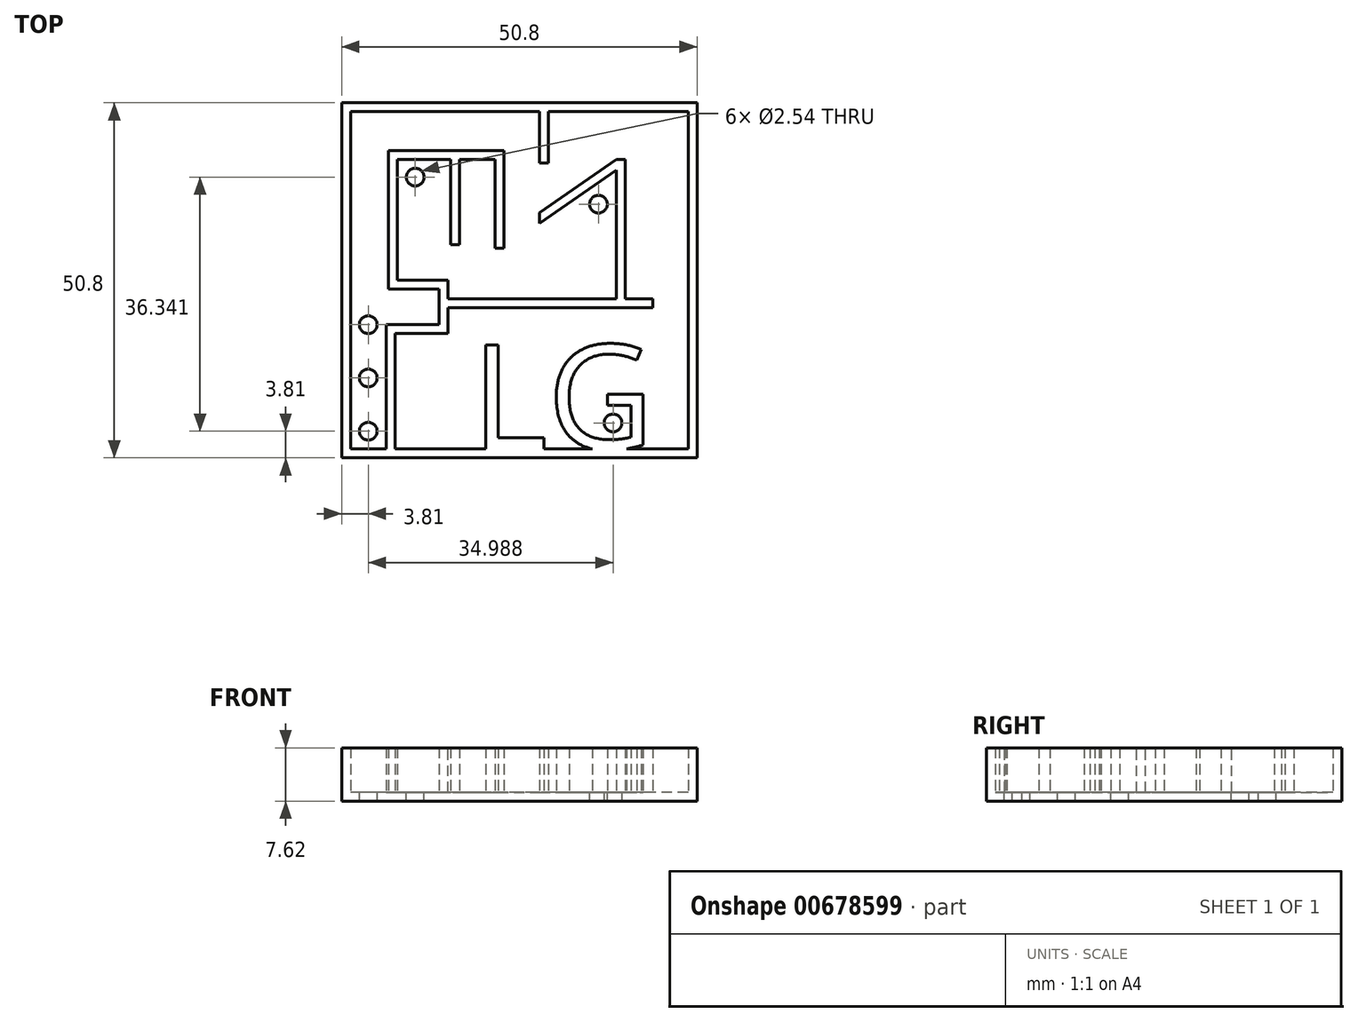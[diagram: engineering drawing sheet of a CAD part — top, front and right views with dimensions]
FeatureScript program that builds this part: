
annotation { "Feature Type Name" : "Feature", "Feature Type Description" : "" }
export const myFeature = defineFeature(function(context is Context, id is Id, definition is map)
    precondition{}
    {
        {
            var Q0;
            Q0=qCreatedBy(makeId("Top.planeOp"),FACE);
            var sketch = newSketch(context, id + "F0", { "sketchPlane" : qUnion([Q0])});
            skLineSegment(sketch, "E0.bottom", {"start": v(0, 0) * mm, "end": v(-50.8, 0) * mm});
            skLineSegment(sketch, "E0.top", {"start": v(0, 50.8) * mm, "end": v(-50.8, 50.8) * mm});
            skLineSegment(sketch, "E0.left", {"start": v(0, 0) * mm, "end": v(0, 50.8) * mm});
            skLineSegment(sketch, "E0.right", {"start": v(-50.8, 0) * mm, "end": v(-50.8, 50.8) * mm});
            skSolve(sketch);
        }
        {
            var Q0;
            Q0=makeQuery(id+"F0.imprint","IMPRINT",FACE,{"disambiguationData":[TD([[makeQuery(id+"F0.imprint","IMPRINT",EDGE,{"derivedFrom":sQuery(id+"F0.wireOp",EDGE,"E0.bottom")}),-1.0]])]});
            extrude(context, id + "F1", {"entities" : qUnion([Q0]), "depth" : 7.62 * mm, "offsetDistance" : 25.4 * mm});
        }
        {
            var Q0;
            Q0=makeQuery(id+"F1.opExtrude","CAP_FACE",FACE,{"disambiguationData":[OSD([sQuery(id+"F0.wireOp",EDGE,"E0.bottom"),sQuery(id+"F0.wireOp",EDGE,"E0.top"),sQuery(id+"F0.wireOp",EDGE,"E0.left"),sQuery(id+"F0.wireOp",EDGE,"E0.right")])],"isStart":false});
            shell(context, id + "F2", {"entities" : qUnion([Q0]), "thickness" : 1.27 * mm});
        }
        {
            var Q0;
            Q0=makeQuery(id+"F2.opShell","OFFSET_FACE",FACE,{"disambiguationData":[OSD([sQuery(id+"F0.wireOp",EDGE,"E0.bottom"),sQuery(id+"F0.wireOp",EDGE,"E0.top"),sQuery(id+"F0.wireOp",EDGE,"E0.left"),sQuery(id+"F0.wireOp",EDGE,"E0.right")])]});
            var sketch = newSketch(context, id + "F3", { "sketchPlane" : qUnion([Q0])});
            skLineSegment(sketch, "E1", {"start": v(-49.53, 1.27) * mm, "end": v(-44.45, 1.27) * mm});
            skLineSegment(sketch, "E2", {"start": v(-44.45, 1.27) * mm, "end": v(-44.45, 19.05) * mm});
            skLineSegment(sketch, "E3", {"start": v(-44.45, 19.05) * mm, "end": v(-43.18, 19.05) * mm});
            skLineSegment(sketch, "E4", {"start": v(-43.18, 19.05) * mm, "end": v(-43.18, 1.27) * mm});
            skSolve(sketch);
        }
        {
            var Q0;
            {var subQ0=sQuery(id+"F3.wireOp",EDGE,"E2");Q0=makeQuery(id+"F3.imprint","IMPRINT",FACE,{"disambiguationData":[TD([[makeQuery(id+"F3.imprint","IMPRINT",EDGE,{"derivedFrom":subQ0}),-1.0]])]});}
            extrude(context, id + "F4", {"entities" : qUnion([Q0]), "operationType" : NewBodyOperationType.ADD, "depth" : 6.35 * mm, "offsetDistance" : 25.4 * mm});
        }
        {
            var Q0;
            Q0=makeQuery(id+"F2.opShell","OFFSET_FACE",FACE,{"disambiguationData":[OSD([sQuery(id+"F0.wireOp",EDGE,"E0.bottom"),sQuery(id+"F0.wireOp",EDGE,"E0.top"),sQuery(id+"F0.wireOp",EDGE,"E0.left"),sQuery(id+"F0.wireOp",EDGE,"E0.right")])]});
            var sketch = newSketch(context, id + "F5", { "sketchPlane" : qUnion([Q0])});
            skLineSegment(sketch, "E5.bottom", {"start": v(-43.18, 19.05) * mm, "end": v(-35.6, 19.05) * mm});
            skLineSegment(sketch, "E5.top", {"start": v(-43.18, 17.78) * mm, "end": v(-35.6, 17.78) * mm});
            skLineSegment(sketch, "E5.left", {"start": v(-43.18, 19.05) * mm, "end": v(-43.18, 17.78) * mm});
            skLineSegment(sketch, "E5.right", {"start": v(-35.6, 19.05) * mm, "end": v(-35.6, 17.78) * mm});
            skSolve(sketch);
        }
        {
            var Q0;
            Q0 = qSketchRegion(id + "F5", true);
            extrude(context, id + "F6", {"entities" : qUnion([Q0]), "operationType" : NewBodyOperationType.ADD, "depth" : 6.35 * mm, "offsetDistance" : 25.4 * mm});
        }
        {
            var Q0;
            Q0=makeQuery(id+"F2.opShell","OFFSET_FACE",FACE,{"disambiguationData":[OSD([sQuery(id+"F0.wireOp",EDGE,"E0.bottom"),sQuery(id+"F0.wireOp",EDGE,"E0.top"),sQuery(id+"F0.wireOp",EDGE,"E0.left"),sQuery(id+"F0.wireOp",EDGE,"E0.right")])]});
            var sketch = newSketch(context, id + "F7", { "sketchPlane" : qUnion([Q0])});
            skLineSegment(sketch, "E6.bottom", {"start": v(-35.6, 19.05) * mm, "end": v(-36.86, 19.05) * mm});
            skLineSegment(sketch, "E6.top", {"start": v(-35.6, 24.13) * mm, "end": v(-36.86, 24.13) * mm});
            skLineSegment(sketch, "E6.left", {"start": v(-35.6, 19.05) * mm, "end": v(-35.6, 24.13) * mm});
            skLineSegment(sketch, "E6.right", {"start": v(-36.86, 19.05) * mm, "end": v(-36.86, 24.13) * mm});
            skSolve(sketch);
        }
        {
            var Q0;
            Q0=makeQuery(id+"F7.imprint","IMPRINT",FACE,{"disambiguationData":[TD([[makeQuery(id+"F7.imprint","IMPRINT",EDGE,{"derivedFrom":sQuery(id+"F7.wireOp",EDGE,"E6.bottom")}),1.0]])]});
            extrude(context, id + "F8", {"entities" : qUnion([Q0]), "operationType" : NewBodyOperationType.ADD, "depth" : 6.35 * mm, "offsetDistance" : 25.4 * mm});
        }
        {
            var Q0;
            Q0=makeQuery(id+"F2.opShell","OFFSET_FACE",FACE,{"disambiguationData":[OSD([sQuery(id+"F0.wireOp",EDGE,"E0.bottom"),sQuery(id+"F0.wireOp",EDGE,"E0.top"),sQuery(id+"F0.wireOp",EDGE,"E0.left"),sQuery(id+"F0.wireOp",EDGE,"E0.right")])]});
            var sketch = newSketch(context, id + "F9", { "sketchPlane" : qUnion([Q0])});
            skLineSegment(sketch, "E7.bottom", {"start": v(-35.6, 24.13) * mm, "end": v(-44.09, 24.13) * mm});
            skLineSegment(sketch, "E7.top", {"start": v(-35.6, 25.4) * mm, "end": v(-44.09, 25.4) * mm});
            skLineSegment(sketch, "E7.left", {"start": v(-35.6, 24.13) * mm, "end": v(-35.6, 25.4) * mm});
            skLineSegment(sketch, "E7.right", {"start": v(-44.09, 24.13) * mm, "end": v(-44.09, 25.4) * mm});
            skSolve(sketch);
        }
        {
            var Q0;
            Q0=makeQuery(id+"F9.imprint","IMPRINT",FACE,{"disambiguationData":[TD([[makeQuery(id+"F9.imprint","IMPRINT",EDGE,{"derivedFrom":sQuery(id+"F9.wireOp",EDGE,"E7.top")}),1.0]])]});
            extrude(context, id + "F10", {"entities" : qUnion([Q0]), "operationType" : NewBodyOperationType.ADD, "depth" : 6.35 * mm, "offsetDistance" : 25.4 * mm});
        }
        {
            var Q0;
            Q0=makeQuery(id+"F2.opShell","OFFSET_FACE",FACE,{"disambiguationData":[OSD([sQuery(id+"F0.wireOp",EDGE,"E0.bottom"),sQuery(id+"F0.wireOp",EDGE,"E0.top"),sQuery(id+"F0.wireOp",EDGE,"E0.left"),sQuery(id+"F0.wireOp",EDGE,"E0.right")])]});
            var sketch = newSketch(context, id + "F11", { "sketchPlane" : qUnion([Q0])});
            skCircle(sketch, "E8", {"center": v(-47, 3.81) * mm, "radius": 1.27 * mm});
            skSolve(sketch);
        }
        {
            var Q0;
            Q0=makeQuery(id+"F11.imprint","IMPRINT",FACE,{"disambiguationData":[TD([[makeQuery(id+"F11.imprint","IMPRINT",EDGE,{"derivedFrom":sQuery(id+"F11.wireOp",EDGE,"E8")}),-1.0]])]});
            var sketch = newSketch(context, id + "F12", { "sketchPlane" : qUnion([Q0])});
            skCircle(sketch, "E9", {"center": v(-47, 11.43) * mm, "radius": 1.27 * mm});
            skSolve(sketch);
        }
        {
            var Q0;
            Q0 = qSketchRegion(id + "F12", true);
            var Q1;
            Q1=makeQuery(id+"F11.imprint","IMPRINT",FACE,{"disambiguationData":[TD([[makeQuery(id+"F11.imprint","IMPRINT",EDGE,{"derivedFrom":sQuery(id+"F11.wireOp",EDGE,"E8")}),1.0]])]});
            extrude(context, id + "F13", {"entities" : qUnion([Q0, Q1]), "operationType" : NewBodyOperationType.REMOVE, "oppositeDirection" : true, "depth" : 25.4 * mm, "offsetDistance" : 25.4 * mm});
        }
        {
            var Q0;
            Q0=makeQuery(id+"F2.opShell","OFFSET_FACE",FACE,{"disambiguationData":[OSD([sQuery(id+"F0.wireOp",EDGE,"E0.bottom"),sQuery(id+"F0.wireOp",EDGE,"E0.top"),sQuery(id+"F0.wireOp",EDGE,"E0.left"),sQuery(id+"F0.wireOp",EDGE,"E0.right")])]});
            var sketch = newSketch(context, id + "F14", { "sketchPlane" : qUnion([Q0])});
            skLineSegment(sketch, "E10.bottom", {"start": v(-44.09, 25.4) * mm, "end": v(-42.82, 25.4) * mm});
            skLineSegment(sketch, "E10.top", {"start": v(-44.09, 42.7) * mm, "end": v(-42.82, 42.7) * mm});
            skLineSegment(sketch, "E10.left", {"start": v(-44.09, 25.4) * mm, "end": v(-44.09, 42.7) * mm});
            skLineSegment(sketch, "E10.right", {"start": v(-42.82, 25.4) * mm, "end": v(-42.82, 42.7) * mm});
            skSolve(sketch);
        }
        {
            var Q0;
            Q0=makeQuery(id+"F14.imprint","IMPRINT",FACE,{"disambiguationData":[TD([[makeQuery(id+"F14.imprint","IMPRINT",EDGE,{"derivedFrom":sQuery(id+"F14.wireOp",EDGE,"E10.bottom")}),-1.0]])]});
            extrude(context, id + "F15", {"entities" : qUnion([Q0]), "operationType" : NewBodyOperationType.ADD, "depth" : 6.35 * mm, "offsetDistance" : 25.4 * mm});
        }
        {
            var Q0;
            Q0=makeQuery(id+"F2.opShell","OFFSET_FACE",FACE,{"disambiguationData":[OSD([sQuery(id+"F0.wireOp",EDGE,"E0.bottom"),sQuery(id+"F0.wireOp",EDGE,"E0.top"),sQuery(id+"F0.wireOp",EDGE,"E0.left"),sQuery(id+"F0.wireOp",EDGE,"E0.right")])]});
            var sketch = newSketch(context, id + "F16", { "sketchPlane" : qUnion([Q0])});
            skLineSegment(sketch, "E11.bottom", {"start": v(-44.09, 42.7) * mm, "end": v(-28.85, 42.7) * mm});
            skLineSegment(sketch, "E11.top", {"start": v(-44.09, 43.96) * mm, "end": v(-28.85, 43.96) * mm});
            skLineSegment(sketch, "E11.left", {"start": v(-44.09, 42.7) * mm, "end": v(-44.09, 43.96) * mm});
            skLineSegment(sketch, "E11.right", {"start": v(-28.85, 42.7) * mm, "end": v(-28.85, 43.96) * mm});
            skSolve(sketch);
        }
        {
            var Q0;
            Q0=makeQuery(id+"F16.imprint","IMPRINT",FACE,{"disambiguationData":[TD([[makeQuery(id+"F16.imprint","IMPRINT",EDGE,{"derivedFrom":sQuery(id+"F16.wireOp",EDGE,"E11.top")}),-1.0]])]});
            extrude(context, id + "F17", {"entities" : qUnion([Q0]), "operationType" : NewBodyOperationType.ADD, "depth" : 6.35 * mm, "offsetDistance" : 25.4 * mm});
        }
        {
            var Q0;
            Q0=makeQuery(id+"F2.opShell","OFFSET_FACE",FACE,{"disambiguationData":[OSD([sQuery(id+"F0.wireOp",EDGE,"E0.bottom"),sQuery(id+"F0.wireOp",EDGE,"E0.top"),sQuery(id+"F0.wireOp",EDGE,"E0.left"),sQuery(id+"F0.wireOp",EDGE,"E0.right")])]});
            var sketch = newSketch(context, id + "F18", { "sketchPlane" : qUnion([Q0])});
            skLineSegment(sketch, "E12.bottom", {"start": v(-28.85, 43.96) * mm, "end": v(-27.58, 43.96) * mm});
            skLineSegment(sketch, "E12.top", {"start": v(-28.85, 30) * mm, "end": v(-27.58, 30) * mm});
            skLineSegment(sketch, "E12.left", {"start": v(-28.85, 43.96) * mm, "end": v(-28.85, 30) * mm});
            skLineSegment(sketch, "E12.right", {"start": v(-27.58, 43.96) * mm, "end": v(-27.58, 30) * mm});
            skSolve(sketch);
        }
        {
            var Q0;
            {var subQ1=sQuery(id+"F18.wireOp",EDGE,"E12.bottom");Q0=makeQuery(id+"F18.imprint","IMPRINT",FACE,{"disambiguationData":[TD([[makeQuery(id+"F18.imprint","IMPRINT",EDGE,{"derivedFrom":subQ1}),-1.0]])]});}
            extrude(context, id + "F19", {"entities" : qUnion([Q0]), "operationType" : NewBodyOperationType.ADD, "depth" : 6.35 * mm, "offsetDistance" : 25.4 * mm});
        }
        {
            var Q0;
            Q0=makeQuery(id+"F2.opShell","OFFSET_FACE",FACE,{"disambiguationData":[OSD([sQuery(id+"F0.wireOp",EDGE,"E0.bottom"),sQuery(id+"F0.wireOp",EDGE,"E0.top"),sQuery(id+"F0.wireOp",EDGE,"E0.left"),sQuery(id+"F0.wireOp",EDGE,"E0.right")])]});
            var sketch = newSketch(context, id + "F20", { "sketchPlane" : qUnion([Q0])});
            skText(sketch, "E13", { "text": "LG", "fontName": "OpenSans-Regular.ttf"});
            const initialGuessF20  = {"E13": [-0.03222, 0.00127, 1, 0, 0.01502]};
            skSetInitialGuess(sketch, initialGuessF20);
            skSolve(sketch);
        }
        {
            var Q0;
            Q0 = qSketchRegion(id + "F20", true);
            extrude(context, id + "F21", {"entities" : qUnion([Q0]), "operationType" : NewBodyOperationType.ADD, "depth" : 6.35 * mm, "offsetDistance" : 25.4 * mm});
        }
        {
            var Q0;
            Q0=makeQuery(id+"F2.opShell","OFFSET_FACE",FACE,{"disambiguationData":[OSD([sQuery(id+"F0.wireOp",EDGE,"E0.bottom"),sQuery(id+"F0.wireOp",EDGE,"E0.top"),sQuery(id+"F0.wireOp",EDGE,"E0.left"),sQuery(id+"F0.wireOp",EDGE,"E0.right")])]});
            var sketch = newSketch(context, id + "F22", { "sketchPlane" : qUnion([Q0])});
            skCircle(sketch, "E14", {"center": v(-12, 4.98) * mm, "radius": 1.27 * mm});
            skSolve(sketch);
        }
        {
            var Q0;
            Q0 = qSketchRegion(id + "F22", true);
            extrude(context, id + "F23", {"entities" : qUnion([Q0]), "operationType" : NewBodyOperationType.REMOVE, "oppositeDirection" : true, "depth" : 25.4 * mm, "offsetDistance" : 25.4 * mm});
        }
        {
            var Q0;
            Q0=makeQuery(id+"F2.opShell","OFFSET_FACE",FACE,{"disambiguationData":[OSD([sQuery(id+"F0.wireOp",EDGE,"E0.bottom"),sQuery(id+"F0.wireOp",EDGE,"E0.top"),sQuery(id+"F0.wireOp",EDGE,"E0.left"),sQuery(id+"F0.wireOp",EDGE,"E0.right")])]});
            var sketch = newSketch(context, id + "F24", { "sketchPlane" : qUnion([Q0])});
            skCircle(sketch, "E15", {"center": v(-47, 19.05) * mm, "radius": 1.27 * mm});
            skSolve(sketch);
        }
        {
            var Q0;
            Q0 = qSketchRegion(id + "F24", true);
            extrude(context, id + "F25", {"entities" : qUnion([Q0]), "operationType" : NewBodyOperationType.REMOVE, "oppositeDirection" : true, "depth" : 25.4 * mm, "offsetDistance" : 25.4 * mm});
        }
        {
            var Q0;
            Q0=makeQuery(id+"F2.opShell","OFFSET_FACE",FACE,{"disambiguationData":[OSD([sQuery(id+"F0.wireOp",EDGE,"E0.bottom"),sQuery(id+"F0.wireOp",EDGE,"E0.top"),sQuery(id+"F0.wireOp",EDGE,"E0.left"),sQuery(id+"F0.wireOp",EDGE,"E0.right")])]});
            var sketch = newSketch(context, id + "F26", { "sketchPlane" : qUnion([Q0])});
            skLineSegment(sketch, "E16", {"start": v(-27.58, 30) * mm, "end": v(-10.82, 41.65) * mm});
            skLineSegment(sketch, "E17", {"start": v(-10.82, 41.65) * mm, "end": v(-11.55, 42.7) * mm});
            skLineSegment(sketch, "E18", {"start": v(-11.55, 42.7) * mm, "end": v(-27.58, 31.54) * mm});
            skSolve(sketch);
        }
        {
            var Q0;
            {var subQ0=sQuery(id+"F26.wireOp",EDGE,"E16");Q0=makeQuery(id+"F26.imprint","IMPRINT",FACE,{"disambiguationData":[TD([[makeQuery(id+"F26.imprint","IMPRINT",EDGE,{"derivedFrom":subQ0}),1.0]])]});}
            extrude(context, id + "F27", {"entities" : qUnion([Q0]), "operationType" : NewBodyOperationType.ADD, "depth" : 6.35 * mm, "offsetDistance" : 25.4 * mm});
        }
        {
            var Q0;
            Q0=makeQuery(id+"F2.opShell","OFFSET_FACE",FACE,{"disambiguationData":[OSD([sQuery(id+"F0.wireOp",EDGE,"E0.bottom"),sQuery(id+"F0.wireOp",EDGE,"E0.top"),sQuery(id+"F0.wireOp",EDGE,"E0.left"),sQuery(id+"F0.wireOp",EDGE,"E0.right")])]});
            var sketch = newSketch(context, id + "F28", { "sketchPlane" : qUnion([Q0])});
            skCircle(sketch, "E19", {"center": v(-40.28, 40.15) * mm, "radius": 1.27 * mm});
            skSolve(sketch);
        }
        {
            var Q0;
            Q0=makeQuery(id+"F28.imprint","IMPRINT",FACE,{"disambiguationData":[TD([[makeQuery(id+"F28.imprint","IMPRINT",EDGE,{"derivedFrom":sQuery(id+"F28.wireOp",EDGE,"E19")}),1.0]])]});
            extrude(context, id + "F29", {"entities" : qUnion([Q0]), "operationType" : NewBodyOperationType.REMOVE, "oppositeDirection" : true, "depth" : 25.4 * mm, "offsetDistance" : 25.4 * mm});
        }
        {
            var Q0;
            Q0=makeQuery(id+"F2.opShell","OFFSET_FACE",FACE,{"disambiguationData":[OSD([sQuery(id+"F0.wireOp",EDGE,"E0.bottom"),sQuery(id+"F0.wireOp",EDGE,"E0.top"),sQuery(id+"F0.wireOp",EDGE,"E0.left"),sQuery(id+"F0.wireOp",EDGE,"E0.right")])]});
            var sketch = newSketch(context, id + "F30", { "sketchPlane" : qUnion([Q0])});
            skLineSegment(sketch, "E20.bottom", {"start": v(-11.55, 42.7) * mm, "end": v(-10.28, 42.7) * mm});
            skLineSegment(sketch, "E20.top", {"start": v(-11.55, 30) * mm, "end": v(-10.28, 30) * mm});
            skLineSegment(sketch, "E20.left", {"start": v(-11.55, 42.7) * mm, "end": v(-11.55, 30) * mm});
            skLineSegment(sketch, "E20.right", {"start": v(-10.28, 42.7) * mm, "end": v(-10.28, 30) * mm});
            skSolve(sketch);
        }
        {
            var Q0;
            Q0 = qSketchRegion(id + "F30", true);
            extrude(context, id + "F31", {"entities" : qUnion([Q0]), "operationType" : NewBodyOperationType.ADD, "depth" : 6.35 * mm, "offsetDistance" : 25.4 * mm});
        }
        {
            var Q0;
            Q0=makeQuery(id+"F2.opShell","OFFSET_FACE",FACE,{"disambiguationData":[OSD([sQuery(id+"F0.wireOp",EDGE,"E0.bottom"),sQuery(id+"F0.wireOp",EDGE,"E0.top"),sQuery(id+"F0.wireOp",EDGE,"E0.left"),sQuery(id+"F0.wireOp",EDGE,"E0.right")])]});
            var sketch = newSketch(context, id + "F32", { "sketchPlane" : qUnion([Q0])});
            skLineSegment(sketch, "E21.bottom", {"start": v(-6.35, 22.72) * mm, "end": v(-25.04, 22.72) * mm});
            skLineSegment(sketch, "E21.top", {"start": v(-6.35, 21.45) * mm, "end": v(-25.04, 21.45) * mm});
            skLineSegment(sketch, "E21.left", {"start": v(-6.35, 22.72) * mm, "end": v(-6.35, 21.45) * mm});
            skLineSegment(sketch, "E21.right", {"start": v(-25.04, 22.72) * mm, "end": v(-25.04, 21.45) * mm});
            skLineSegment(sketch, "E22.bottom", {"start": v(-10.28, 30) * mm, "end": v(-11.55, 30) * mm});
            skLineSegment(sketch, "E22.top", {"start": v(-10.28, 30) * mm, "end": v(-11.55, 30) * mm});
            skLineSegment(sketch, "E22.left", {"start": v(-10.28, 30) * mm, "end": v(-10.28, 30) * mm});
            skLineSegment(sketch, "E22.right", {"start": v(-11.55, 30) * mm, "end": v(-11.55, 30) * mm});
            skLineSegment(sketch, "E23.top", {"start": v(-10.28, 22.72) * mm, "end": v(-11.55, 22.72) * mm});
            skLineSegment(sketch, "E23.left", {"start": v(-10.28, 30) * mm, "end": v(-10.28, 22.72) * mm});
            skLineSegment(sketch, "E23.right", {"start": v(-11.55, 30) * mm, "end": v(-11.55, 22.72) * mm});
            skSolve(sketch);
        }
        {
            var Q0;
            Q0 = qSketchRegion(id + "F32", true);
            extrude(context, id + "F33", {"entities" : qUnion([Q0]), "operationType" : NewBodyOperationType.ADD, "depth" : 6.35 * mm, "offsetDistance" : 25.4 * mm});
        }
        {
            var Q0;
            Q0=makeQuery(id+"F2.opShell","OFFSET_FACE",FACE,{"disambiguationData":[OSD([sQuery(id+"F0.wireOp",EDGE,"E0.bottom"),sQuery(id+"F0.wireOp",EDGE,"E0.top"),sQuery(id+"F0.wireOp",EDGE,"E0.left"),sQuery(id+"F0.wireOp",EDGE,"E0.right")])]});
            var sketch = newSketch(context, id + "F34", { "sketchPlane" : qUnion([Q0])});
            skCircle(sketch, "E24", {"center": v(-14.09, 36.28) * mm, "radius": 1.27 * mm});
            skSolve(sketch);
        }
        {
            var Q0;
            Q0 = qSketchRegion(id + "F34", true);
            extrude(context, id + "F35", {"entities" : qUnion([Q0]), "operationType" : NewBodyOperationType.REMOVE, "depth" : 6.35 * mm, "offsetDistance" : 25.4 * mm});
        }
        {
            var Q0;
            Q0 = qSketchRegion(id + "F34", true);
            extrude(context, id + "F36", {"entities" : qUnion([Q0]), "operationType" : NewBodyOperationType.REMOVE, "oppositeDirection" : true, "depth" : 25.4 * mm, "offsetDistance" : 25.4 * mm});
        }
        {
            var Q0;
            Q0=makeQuery(id+"F2.opShell","OFFSET_FACE",FACE,{"disambiguationData":[OSD([sQuery(id+"F0.wireOp",EDGE,"E0.bottom"),sQuery(id+"F0.wireOp",EDGE,"E0.top"),sQuery(id+"F0.wireOp",EDGE,"E0.left"),sQuery(id+"F0.wireOp",EDGE,"E0.right")])]});
            var sketch = newSketch(context, id + "F37", { "sketchPlane" : qUnion([Q0])});
            skLineSegment(sketch, "E25", {"start": v(-28.85, 42.7) * mm, "end": v(-33.93, 42.7) * mm});
            skLineSegment(sketch, "E26.bottom", {"start": v(-33.93, 42.7) * mm, "end": v(-35.2, 42.7) * mm});
            skLineSegment(sketch, "E26.top", {"start": v(-33.93, 30.48) * mm, "end": v(-35.2, 30.48) * mm});
            skLineSegment(sketch, "E26.left", {"start": v(-33.93, 42.7) * mm, "end": v(-33.93, 30.48) * mm});
            skLineSegment(sketch, "E26.right", {"start": v(-35.2, 42.7) * mm, "end": v(-35.2, 30.48) * mm});
            skSolve(sketch);
        }
        {
            var Q0;
            Q0 = qSketchRegion(id + "F37", true);
            extrude(context, id + "F38", {"entities" : qUnion([Q0]), "operationType" : NewBodyOperationType.ADD, "depth" : 6.35 * mm, "offsetDistance" : 25.4 * mm});
        }
        {
            var Q0;
            Q0=makeQuery(id+"F2.opShell","OFFSET_FACE",FACE,{"disambiguationData":[OSD([sQuery(id+"F0.wireOp",EDGE,"E0.bottom"),sQuery(id+"F0.wireOp",EDGE,"E0.top"),sQuery(id+"F0.wireOp",EDGE,"E0.left"),sQuery(id+"F0.wireOp",EDGE,"E0.right")])]});
            var sketch = newSketch(context, id + "F39", { "sketchPlane" : qUnion([Q0])});
            skLineSegment(sketch, "E27.bottom", {"start": v(-22.5, 49.53) * mm, "end": v(-21.23, 49.53) * mm});
            skLineSegment(sketch, "E27.top", {"start": v(-22.5, 42.15) * mm, "end": v(-21.23, 42.15) * mm});
            skLineSegment(sketch, "E27.left", {"start": v(-22.5, 49.53) * mm, "end": v(-22.5, 42.15) * mm});
            skLineSegment(sketch, "E27.right", {"start": v(-21.23, 49.53) * mm, "end": v(-21.23, 42.15) * mm});
            skSolve(sketch);
        }
        {
            var Q0;
            Q0 = qSketchRegion(id + "F39", true);
            extrude(context, id + "F40", {"entities" : qUnion([Q0]), "operationType" : NewBodyOperationType.ADD, "depth" : 6.35 * mm, "offsetDistance" : 25.4 * mm});
        }
        {
            var Q0;
            Q0=makeQuery(id+"F33.opExtrude","SWEPT_FACE",FACE,{"disambiguationData":[OSD([sQuery(id+"F32.wireOp",EDGE,"E21.right")])]});
            extrude(context, id + "F41", {"entities" : qUnion([Q0]), "operationType" : NewBodyOperationType.ADD, "endBound" : BoundingType.UP_TO_NEXT, "depth" : 25.4 * mm, "offsetDistance" : 25.4 * mm});
        }
        {
            var Q0;
            {var subQ1=sQuery(id+"F0.wireOp",EDGE,"E0.right");var subQ3=sQuery(id+"F0.wireOp",EDGE,"E0.top");Q0=makeQuery(id+"F40.boolean.opBoolean","SPLIT",FACE,{"disambiguationData":[TD([makeQuery(id+"F2.opShell","OFFSET_FACE",FACE,{"disambiguationData":[OSD([subQ1])]})])],"derivedFrom":makeQuery(id+"F2.opShell","OFFSET_FACE",FACE,{"disambiguationData":[OSD([subQ3])]})});}
            var sketch = newSketch(context, id + "F42", { "sketchPlane" : qUnion([Q0])});
            skLineSegment(sketch, "E28.bottom", {"start": v(-22.5, 1.27) * mm, "end": v(-27.58, 1.27) * mm});
            skLineSegment(sketch, "E28.top", {"start": v(-22.5, 7.62) * mm, "end": v(-27.58, 7.62) * mm});
            skLineSegment(sketch, "E28.left", {"start": v(-22.5, 1.27) * mm, "end": v(-22.5, 7.62) * mm});
            skLineSegment(sketch, "E28.right", {"start": v(-27.58, 1.27) * mm, "end": v(-27.58, 7.62) * mm});
            skSolve(sketch);
        }
        {
            var Q0;
            Q0 = qSketchRegion(id + "F42", true);
            extrude(context, id + "F43", {"entities" : qUnion([Q0]), "operationType" : NewBodyOperationType.REMOVE, "depth" : 25.4 * mm, "offsetDistance" : 25.4 * mm});
        }
    });
